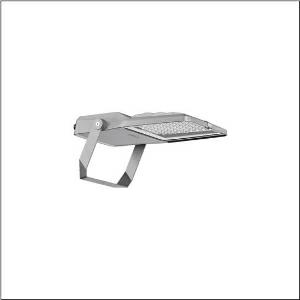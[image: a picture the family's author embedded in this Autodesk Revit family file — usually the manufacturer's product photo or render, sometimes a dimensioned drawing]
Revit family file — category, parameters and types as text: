
# Revit family: floodlight_fl_21_iq_mini___pl61_5xa7772c3c1a_b73e
name_source: partatom
category: Lighting Fixtures
units: mm (PartAtom-declared; Revit-internal decimal feet)

## family parameters
Cut with Voids When Loaded = No
Host = Face
Light Source = No
Part Type = Normal
Room Calculation Point = No
Round Connector Dimension = Use Diameter
Shared = No

## types (1)
- --- (1 x LED, 10320 lm, 87.2 W, 3000K)
    Apparent Load = 87 VA
    CIE Flux Codes = 33 65 98 100 100
    Color Rendering = 80
    Color Temperature = 3000K
    Default Elevation = 1800 mm
    Description = Floodlight FL 21 iQ mini, floodlight, primary light control with lens, of PMMA, primary optical cover: protective disc, of toughened safety glass, transparent, light distribution: PL61, light emission: direct distribution, installation type: surface-mounted, LED, High Power LED, rated luminous flux: 10.320lm, luminous efficacy: 118lm/W, light colour: 830, colour temperature: 3000K, control gear: iQ Street-Remote/DALI, control: Street-Remote, Auto-Match, Temp-Guard, Night-Set, Smart-Wire, Desk-Remote (wireless, voltage-free reading and setting of iQ features in the workshop via application-optimized NFC function/RFID function), optimised constant luminous flux control (CLO 2.0), with terminal, 6-pole, mains connection: 220..240V, AC, 50/60Hz, start of lifetime: 87W, end of service life: 92W, reduction: 40W, luminaire housing, of diecast aluminium, powder-coated, Siteco® metallic grey (DB 702S), corrosivity category C5 mid according to DIN EN ISO 12944, suitable for swimming pools, chlorine-resistant, sealing non-destructively replaceable, mounting bracket, of steel, galvanised, powder-coated, Siteco® metallic grey (DB 702S), protection rating (complete): IP66, insulation class (complete): insulation class II (safety insulation), certification: CE, ENEC, VDE, protection symbol: D, impact resistance: IK08, permissible operating ambient temperature: -40..+40°C, permissible operating ambient temperature for outdoor applications: -40..+50°C, standard: DIN EN 12944, LABS conformity tested according to VDMA 24364:2018-05, packaging unit: 1 piece

Light Distribution: PL61
    Height = 70 mm
    Lamp = 1 x LED
    Lamp Light Flux = 10320 lm
    Lamp Power = 87.2 W
    Lamp count = 1
    Length = 485 mm
    Luminous efficacy = 118 lm/W
    Manufacturer = Siteco
    ModVariant = No
    Model = 5XA7772C3C1A
    Number of Poles = 1
    OnlyDefault = Yes
    Power Factor = 1
    Product Name = Floodlight FL 21 iQ mini | PL61
    Product group = floodlight | pylon annexe
    ProductGroupID = 6200
    Protection Class = Protection class II
    Protection Degree = IP 66
    RLX_Detail_Level = 1
    RLX_Emergency_Light_Flux = 0 lm
    RLX_Emergency_Type = 0
    RLX_Emergency_Type_DB = No
    RlxData = <blob elided: 96361 chars, md5=43d4c78e>
    Socket = socket
    Standby Power = 0 W
    System Light Flux = 10320 lm
    System Power = 87 W
    Type Comments = factory setting: luminous flux: 100 % | dim-lin: 254 | 456 mA
    Type Image = l_1006845.jpg
    URL = http://relux.com
    VarID = @adj_173008
    Voltage = 0 V
    Weight = 0.00 kg
    Width = 337 mm

## geometry (parser evidence)
native form markers: Blend x4, Sweep x13
no freeform markers — native parametric forms only
